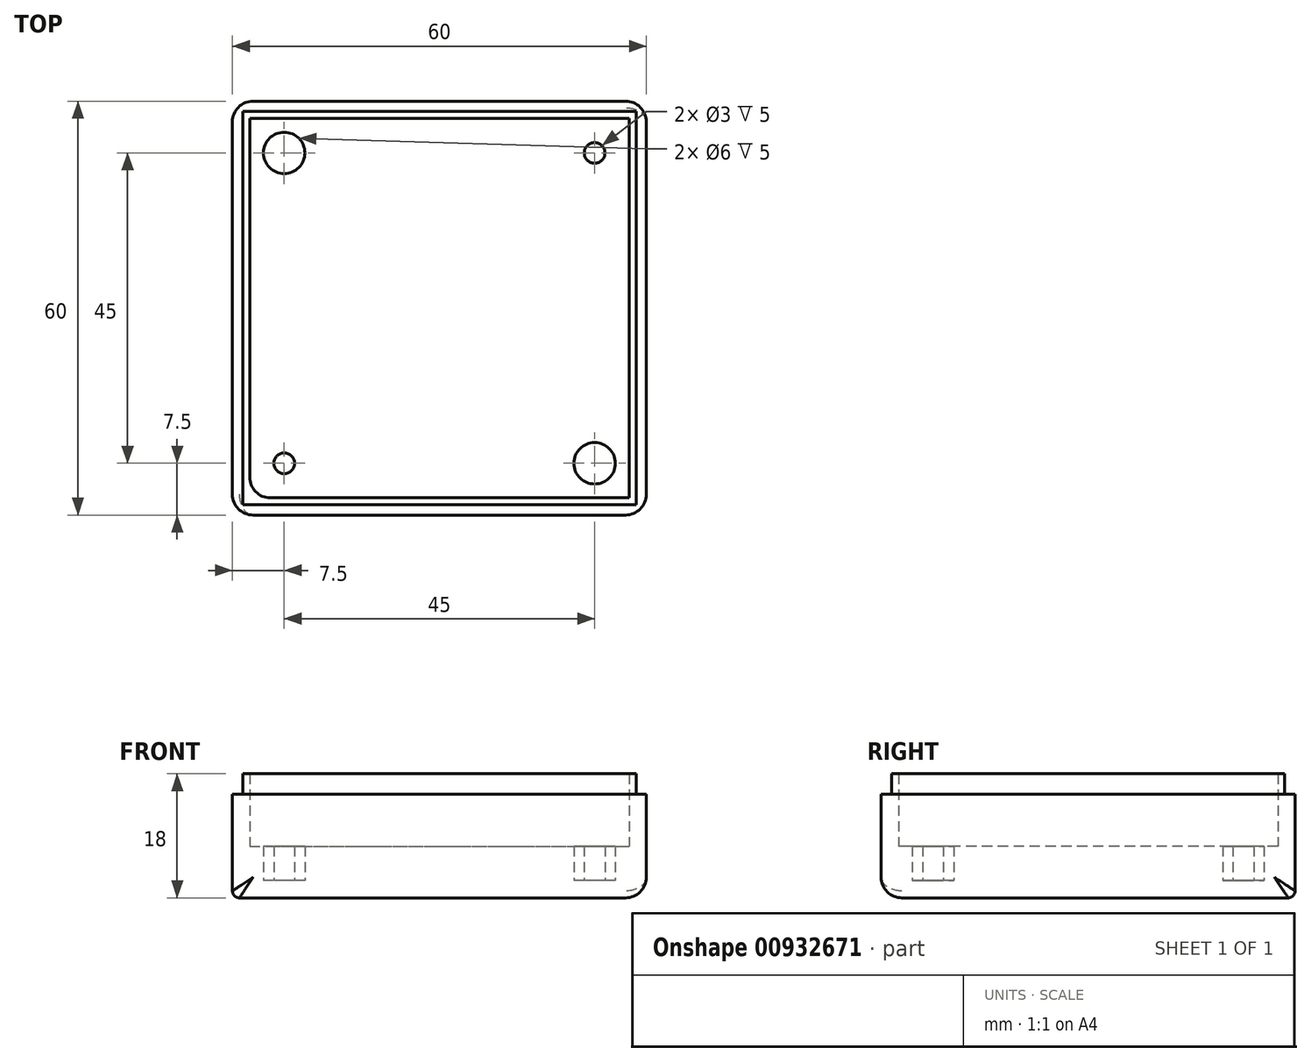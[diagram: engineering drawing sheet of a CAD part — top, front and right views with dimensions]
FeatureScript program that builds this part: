
annotation { "Feature Type Name" : "Feature", "Feature Type Description" : "" }
export const myFeature = defineFeature(function(context is Context, id is Id, definition is map)
    precondition{}
    {
        {
            var Q0;
            Q0=qCreatedBy(makeId("Top.planeOp"),FACE);
            var sketch = newSketch(context, id + "F0", { "sketchPlane" : qUnion([Q0])});
            skLineSegment(sketch, "E0.bottom", {"start": v(-27.5, 27.5) * mm, "end": v(27.5, 27.5) * mm});
            skLineSegment(sketch, "E0.top", {"start": v(-27.5, -27.5) * mm, "end": v(27.5, -27.5) * mm});
            skLineSegment(sketch, "E0.left", {"start": v(-27.5, 27.5) * mm, "end": v(-27.5, -27.5) * mm});
            skLineSegment(sketch, "E0.right", {"start": v(27.5, 27.5) * mm, "end": v(27.5, -27.5) * mm});
            skLineSegment(sketch, "E1.bottom", {"start": v(-30, 30) * mm, "end": v(30, 30) * mm});
            skLineSegment(sketch, "E1.top", {"start": v(-30, -30) * mm, "end": v(30, -30) * mm});
            skLineSegment(sketch, "E1.left", {"start": v(-30, 30) * mm, "end": v(-30, -30) * mm});
            skLineSegment(sketch, "E1.right", {"start": v(30, 30) * mm, "end": v(30, -30) * mm});
            skSolve(sketch);
        }
        {
            var Q0;
            Q0=makeQuery(id+"F0.imprint","IMPRINT",FACE,{"disambiguationData":[TD([[makeQuery(id+"F0.imprint","IMPRINT",EDGE,{"derivedFrom":sQuery(id+"F0.wireOp",EDGE,"E0.bottom")}),1.0]])]});
            extrude(context, id + "F1", {"entities" : qUnion([Q0]), "depth" : 15 * mm, "offsetDistance" : 25 * mm});
        }
        {
            var Q0;
            Q0=qCreatedBy(makeId("Top.planeOp"),FACE);
            var sketch = newSketch(context, id + "F2", { "sketchPlane" : qUnion([Q0])});
            skLineSegment(sketch, "E2.bottom", {"start": v(-30, -30) * mm, "end": v(30, -30) * mm});
            skLineSegment(sketch, "E2.top", {"start": v(-30, 30) * mm, "end": v(30, 30) * mm});
            skLineSegment(sketch, "E2.left", {"start": v(-30, -30) * mm, "end": v(-30, 30) * mm});
            skLineSegment(sketch, "E2.right", {"start": v(30, -30) * mm, "end": v(30, 30) * mm});
            skSolve(sketch);
        }
        {
            var Q0;
            Q0=makeQuery(id+"F2.imprint","IMPRINT",FACE,{"disambiguationData":[TD([[makeQuery(id+"F2.imprint","IMPRINT",EDGE,{"derivedFrom":sQuery(id+"F2.wireOp",EDGE,"E2.bottom")}),1.0]])]});
            extrude(context, id + "F3", {"entities" : qUnion([Q0]), "operationType" : NewBodyOperationType.ADD, "depth" : 2.5 * mm, "offsetDistance" : 25 * mm});
        }
        {
            var Q0;
            Q0=makeQuery(id+"F3.opExtrude","CAP_EDGE",EDGE,{"disambiguationData":[OSD([sQuery(id+"F2.wireOp",EDGE,"E2.right")])],"isStart":true});
            var Q1;
            Q1=makeQuery(id+"F3.opExtrude","CAP_EDGE",EDGE,{"disambiguationData":[OSD([sQuery(id+"F2.wireOp",EDGE,"E2.bottom")])],"isStart":true});
            var Q2;
            Q2=makeQuery(id+"F1.opExtrude","CAP_EDGE",EDGE,{"disambiguationData":[OSD([sQuery(id+"F0.wireOp",EDGE,"E1.left")])],"isStart":true});
            var Q3;
            Q3=makeQuery(id+"F1.opExtrude","CAP_EDGE",EDGE,{"disambiguationData":[OSD([sQuery(id+"F0.wireOp",EDGE,"E1.bottom")])],"isStart":true});
            fillet(context, id + "F4", {"entities" : qUnion([Q0, Q1, Q2, Q3]), "tangentPropagation" : true, "radius" : 1 * mm, "defaultsChanged" : true, "vertexSettings" : [], "allowEdgeOverflow" : false});
        }
        {
            var Q0;
            Q0=makeQuery(id+"F1.opExtrude","CAP_EDGE",EDGE,{"disambiguationData":[OSD([sQuery(id+"F0.wireOp",EDGE,"E1.top")])],"isStart":true});
            var Q1;
            Q1=makeQuery(id+"F1.opExtrude","CAP_EDGE",EDGE,{"disambiguationData":[OSD([sQuery(id+"F0.wireOp",EDGE,"E1.right")])],"isStart":true});
            var Q2;
            Q2=makeQuery(id+"F1.opExtrude","SWEPT_EDGE",EDGE,{"disambiguationData":[OSD([sQuery(id+"F0.wireOp",EDGE,"E1.top"),sQuery(id+"F0.wireOp",EDGE,"E1.left")])]});
            var Q3;
            Q3=makeQuery(id+"F1.opExtrude","SWEPT_EDGE",EDGE,{"disambiguationData":[OSD([sQuery(id+"F0.wireOp",EDGE,"E1.top"),sQuery(id+"F0.wireOp",EDGE,"E1.right")])]});
            var Q4;
            Q4=makeQuery(id+"F1.opExtrude","SWEPT_EDGE",EDGE,{"disambiguationData":[OSD([sQuery(id+"F0.wireOp",EDGE,"E0.top"),sQuery(id+"F0.wireOp",EDGE,"E0.left")])]});
            var Q5;
            Q5=makeQuery(id+"F1.opExtrude","SWEPT_EDGE",EDGE,{"disambiguationData":[OSD([sQuery(id+"F0.wireOp",EDGE,"E1.bottom"),sQuery(id+"F0.wireOp",EDGE,"E1.left")])]});
            fillet(context, id + "F5", {"entities" : qUnion([Q0, Q1, Q2, Q3, Q4, Q5]), "tangentPropagation" : true, "radius" : 3 * mm, "defaultsChanged" : true, "vertexSettings" : [], "allowEdgeOverflow" : false});
        }
        {
            var Q0;
            Q0=makeQuery(id+"F3.opExtrude","CAP_FACE",FACE,{"disambiguationData":[OSD([sQuery(id+"F2.wireOp",EDGE,"E2.bottom"),sQuery(id+"F2.wireOp",EDGE,"E2.top"),sQuery(id+"F2.wireOp",EDGE,"E2.left"),sQuery(id+"F2.wireOp",EDGE,"E2.right")])],"isStart":false});
            var sketch = newSketch(context, id + "F6", { "sketchPlane" : qUnion([Q0])});
            skSolve(sketch);
        }
        {
            var Q0;
            {var subQ0=makeQuery(id+"F3.opExtrude","CAP_FACE",FACE,{"disambiguationData":[OSD([sQuery(id+"F2.wireOp",EDGE,"E2.bottom"),sQuery(id+"F2.wireOp",EDGE,"E2.top"),sQuery(id+"F2.wireOp",EDGE,"E2.left"),sQuery(id+"F2.wireOp",EDGE,"E2.right")])],"isStart":false});Q0=makeQuery(id+"F6.imprint","IMPRINT",FACE,{"disambiguationData":[TD([[makeQuery(id+"F6.imprint","IMPRINT",EDGE,{"derivedFrom":makeQuery(id+"F3.boolean.opBoolean","INTERSECT",EDGE,{"derivedFrom":[makeQuery(id+"F1.opExtrude","SWEPT_FACE",FACE,{"disambiguationData":[OSD([sQuery(id+"F0.wireOp",EDGE,"E0.bottom")])]}),subQ0]})}),-1.0]])]});}
            var sketch = newSketch(context, id + "F7", { "sketchPlane" : qUnion([Q0])});
            skCircle(sketch, "E3", {"center": v(22.5, 22.5) * mm, "radius": 1.5 * mm});
            skCircle(sketch, "E4", {"center": v(22.5, 22.5) * mm, "radius": 3 * mm});
            skCircle(sketch, "E5.MirrorC", {"center": v(22.5, -22.5) * mm, "radius": 3 * mm});
            skCircle(sketch, "E6.MirrorC", {"center": v(22.5, -22.5) * mm, "radius": 1.5 * mm});
            skCircle(sketch, "E7.MirrorC", {"center": v(-22.5, -22.5) * mm, "radius": 3 * mm});
            skCircle(sketch, "E8.MirrorC", {"center": v(-22.5, -22.5) * mm, "radius": 1.5 * mm});
            skCircle(sketch, "E9.MirrorC", {"center": v(-22.5, 22.5) * mm, "radius": 3 * mm});
            skCircle(sketch, "E10.MirrorC", {"center": v(-22.5, 22.5) * mm, "radius": 1.5 * mm});
            skSolve(sketch);
        }
        {
            var Q0;
            Q0=makeQuery(id+"F7.imprint","IMPRINT",FACE,{"disambiguationData":[TD([[makeQuery(id+"F7.imprint","IMPRINT",EDGE,{"derivedFrom":sQuery(id+"F7.wireOp",EDGE,"E9.MirrorC")}),-1.0]])]});
            var Q1;
            Q1=makeQuery(id+"F7.imprint","IMPRINT",FACE,{"disambiguationData":[TD([[makeQuery(id+"F7.imprint","IMPRINT",EDGE,{"derivedFrom":sQuery(id+"F7.wireOp",EDGE,"E3")}),-1.0]])]});
            var Q2;
            Q2=makeQuery(id+"F7.imprint","IMPRINT",FACE,{"disambiguationData":[TD([[makeQuery(id+"F7.imprint","IMPRINT",EDGE,{"derivedFrom":sQuery(id+"F7.wireOp",EDGE,"E5.MirrorC")}),-1.0]])]});
            var Q3;
            Q3=makeQuery(id+"F7.imprint","IMPRINT",FACE,{"disambiguationData":[TD([[makeQuery(id+"F7.imprint","IMPRINT",EDGE,{"derivedFrom":sQuery(id+"F7.wireOp",EDGE,"E7.MirrorC")}),1.0]])]});
            extrude(context, id + "F8", {"entities" : qUnion([Q0, Q1, Q2, Q3]), "operationType" : NewBodyOperationType.ADD, "depth" : 5 * mm, "offsetDistance" : 25 * mm});
        }
        {
            var Q0;
            Q0=makeQuery(id+"F1.opExtrude","CAP_FACE",FACE,{"disambiguationData":[OSD([sQuery(id+"F0.wireOp",EDGE,"E0.bottom"),sQuery(id+"F0.wireOp",EDGE,"E0.top"),sQuery(id+"F0.wireOp",EDGE,"E0.left"),sQuery(id+"F0.wireOp",EDGE,"E0.right"),sQuery(id+"F0.wireOp",EDGE,"E1.bottom"),sQuery(id+"F0.wireOp",EDGE,"E1.top"),sQuery(id+"F0.wireOp",EDGE,"E1.left"),sQuery(id+"F0.wireOp",EDGE,"E1.right")])],"isStart":false});
            var sketch = newSketch(context, id + "F9", { "sketchPlane" : qUnion([Q0])});
            skLineSegment(sketch, "E11.bottom", {"start": v(-28.5, 28.5) * mm, "end": v(28.5, 28.5) * mm});
            skLineSegment(sketch, "E11.top", {"start": v(-28.5, -28.5) * mm, "end": v(28.5, -28.5) * mm});
            skLineSegment(sketch, "E11.left", {"start": v(-28.5, 28.5) * mm, "end": v(-28.5, -28.5) * mm});
            skLineSegment(sketch, "E11.right", {"start": v(28.5, 28.5) * mm, "end": v(28.5, -28.5) * mm});
            skPoint(sketch, "E11.middle", {"position": v(0, 0) * mm});
            skSolve(sketch);
        }
        {
            var Q0;
            Q0=makeQuery(id+"F9.imprint","IMPRINT",FACE,{"disambiguationData":[TD([[makeQuery(id+"F9.imprint","IMPRINT",EDGE,{"derivedFrom":sQuery(id+"F9.wireOp",EDGE,"E11.bottom")}),-1.0]])]});
            extrude(context, id + "F10", {"entities" : qUnion([Q0]), "operationType" : NewBodyOperationType.ADD, "depth" : 3 * mm, "offsetDistance" : 25 * mm});
        }
    });
